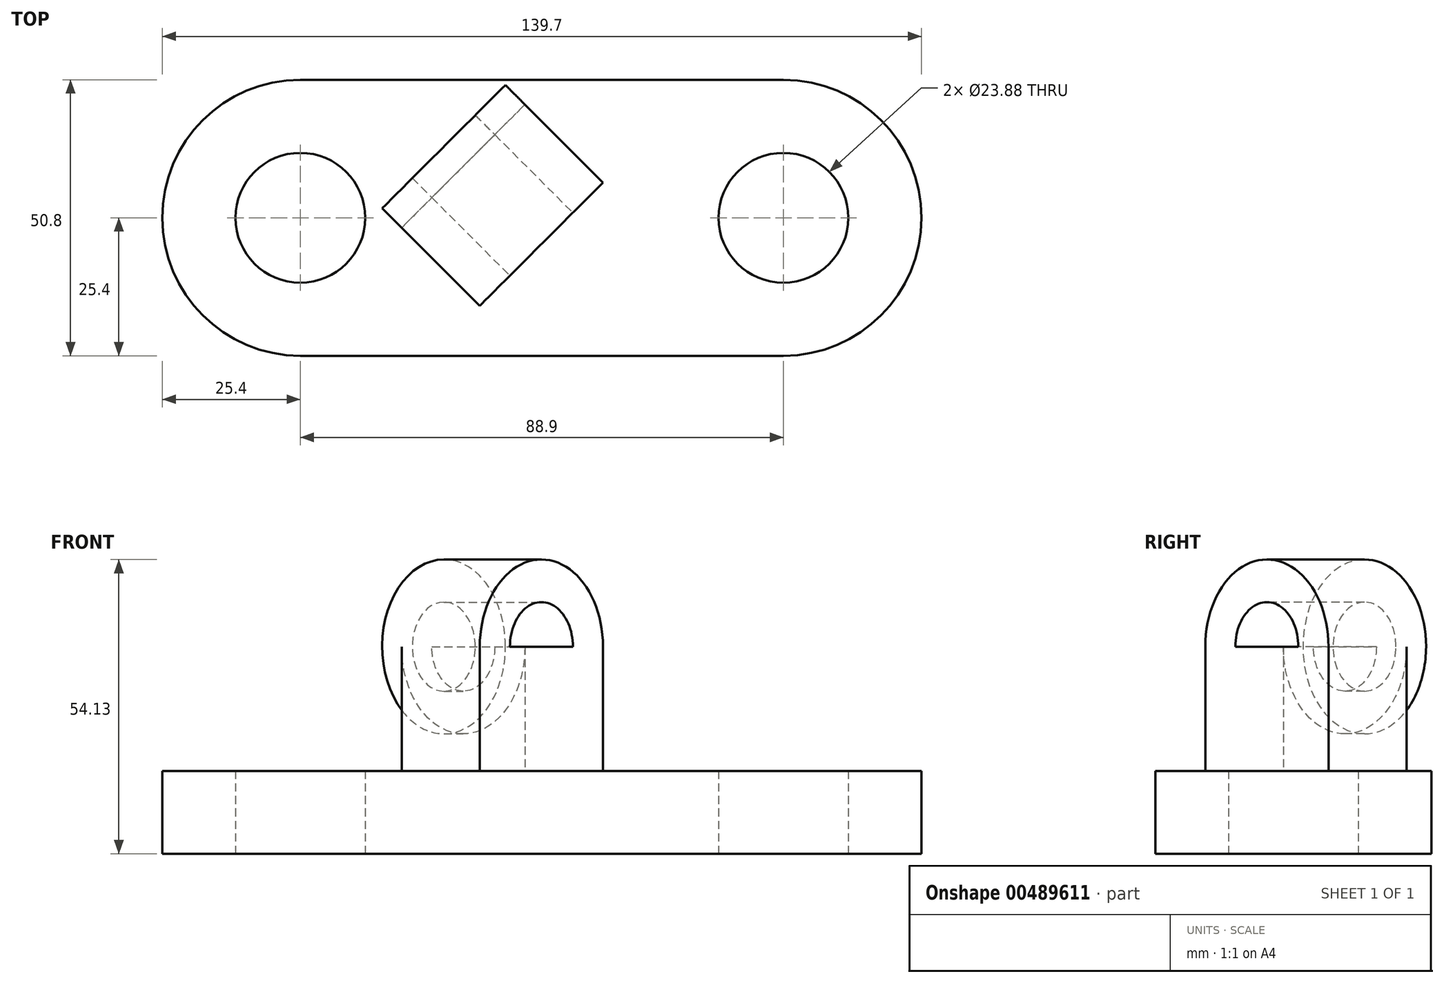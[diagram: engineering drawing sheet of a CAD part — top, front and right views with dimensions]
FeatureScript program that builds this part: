
annotation { "Feature Type Name" : "Feature", "Feature Type Description" : "" }
export const myFeature = defineFeature(function(context is Context, id is Id, definition is map)
    precondition{}
    {
        {
            var Q0;
            Q0=qCreatedBy(makeId("Top.planeOp"),FACE);
            var sketch = newSketch(context, id + "F0", { "sketchPlane" : qUnion([Q0])});
            skLineSegment(sketch, "E0.bottom", {"start": v(44.45, -25.4) * mm, "end": v(-44.45, -25.4) * mm});
            skLineSegment(sketch, "E0.top", {"start": v(44.45, 25.4) * mm, "end": v(-44.45, 25.4) * mm});
            skPoint(sketch, "E0.middle", {"position": v(0, 0) * mm});
            skArc(sketch, "E1", {"start": v(-44.45, 25.4) * mm, "mid": v(-69.85, 0) * mm, "end": v(-44.45, -25.4) * mm});
            skArc(sketch, "E2", {"start": v(44.45, -25.4) * mm, "mid": v(69.85, 0) * mm, "end": v(44.45, 25.4) * mm});
            skCircle(sketch, "E3", {"center": v(44.45, 0) * mm, "radius": 6.74 * mm});
            skCircle(sketch, "E4", {"center": v(-44.45, 0) * mm, "radius": 6.74 * mm});
            skCircle(sketch, "E5", {"center": v(44.45, 0) * mm, "radius": 11.94 * mm});
            skCircle(sketch, "E6", {"center": v(-44.45, 0) * mm, "radius": 11.94 * mm});
            skLineSegment(sketch, "E7", {"start": v(-25.8, -1.84) * mm, "end": v(-3.12, 20.83) * mm});
            skLineSegment(sketch, "E8", {"start": v(-3.12, 20.83) * mm, "end": v(11.24, 6.47) * mm});
            skLineSegment(sketch, "E9", {"start": v(11.24, 6.47) * mm, "end": v(-11.43, -16.2) * mm});
            skLineSegment(sketch, "E10", {"start": v(-11.43, -16.2) * mm, "end": v(-25.8, -1.84) * mm});
            skSolve(sketch);
        }
        {
            var Q0;
            Q0=makeQuery(id+"F0.imprint","IMPRINT",FACE,{"disambiguationData":[TD([[makeQuery(id+"F0.imprint","IMPRINT",EDGE,{"derivedFrom":sQuery(id+"F0.wireOp",EDGE,"E0.bottom")}),-1.0]])]});
            extrude(context, id + "F1", {"entities" : qUnion([Q0]), "depth" : 15.24 * mm});
        }
        {
            var Q0;
            Q0=makeQuery(id+"F0.imprint","IMPRINT",FACE,{"disambiguationData":[TD([[makeQuery(id+"F0.imprint","IMPRINT",EDGE,{"derivedFrom":sQuery(id+"F0.wireOp",EDGE,"E7")}),-1.0]])]});
            extrude(context, id + "F2", {"entities" : qUnion([Q0]), "operationType" : NewBodyOperationType.ADD, "depth" : 38.1 * mm});
        }
        {
            var Q0;
            Q0=makeQuery(id+"F2.opExtrude","SWEPT_FACE",FACE,{"disambiguationData":[OSD([sQuery(id+"F0.wireOp",EDGE,"E9")])]});
            var sketch = newSketch(context, id + "F3", { "sketchPlane" : qUnion([Q0])});
            skCircle(sketch, "E11", {"center": v(-3.5, 38.1) * mm, "radius": 16.03 * mm});
            skCircle(sketch, "E12", {"center": v(-3.5, 38.1) * mm, "radius": 8.2 * mm});
            skSolve(sketch);
        }
        {
            var Q0;
            Q0 = qSketchRegion(id + "F3", true);
            extrude(context, id + "F4", {"entities" : qUnion([Q0]), "operationType" : NewBodyOperationType.ADD, "oppositeDirection" : true, "depth" : 25.4 * mm});
        }
    });
